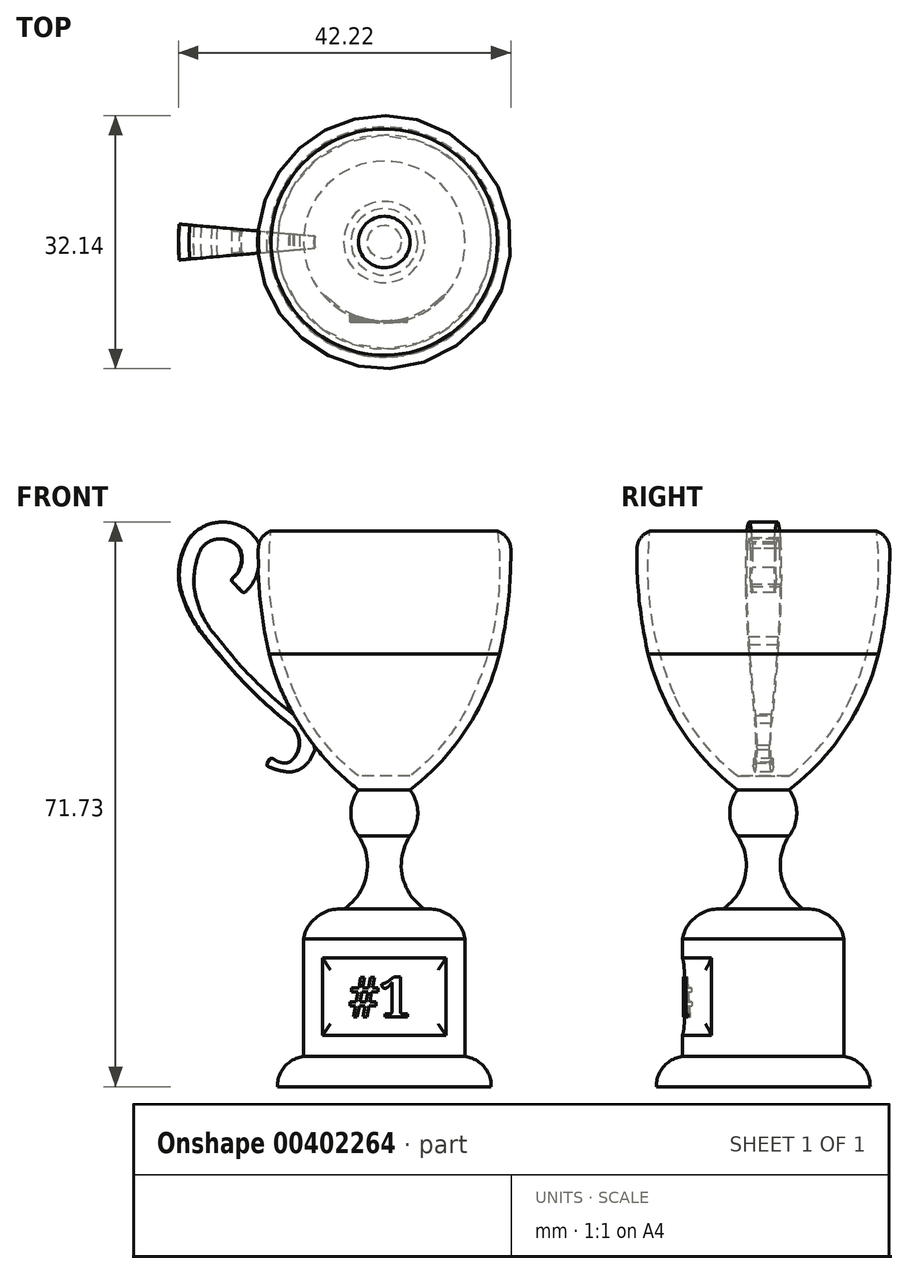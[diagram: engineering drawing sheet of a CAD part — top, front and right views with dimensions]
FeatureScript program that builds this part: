
annotation { "Feature Type Name" : "Feature", "Feature Type Description" : "" }
export const myFeature = defineFeature(function(context is Context, id is Id, definition is map)
    precondition{}
    {
        {
            var Q0;
            Q0=qCreatedBy(makeId("Front.planeOp"),FACE);
            var sketch = newSketch(context, id + "F0", { "sketchPlane" : qUnion([Q0])});
            skArc(sketch, "E0", {"start": v(-16, 36.3) * mm, "mid": v(-15.85, 28.37) * mm, "end": v(-14.63, 20.54) * mm});
            skArc(sketch, "E1", {"start": v(-14.63, 20.54) * mm, "mid": v(-10.4, 10.97) * mm, "end": v(-3.26, 3.3) * mm});
            skArc(sketch, "E2", {"start": v(-3.26, 3.3) * mm, "mid": v(-4.26, 0.37) * mm, "end": v(-3.26, -2.57) * mm});
            skArc(sketch, "E3", {"start": v(-5.16, -11.85) * mm, "mid": v(-2.29, -7.6) * mm, "end": v(-3.26, -2.57) * mm});
            skArc(sketch, "E4", {"start": v(-5.16, -11.85) * mm, "mid": v(-8.46, -12.75) * mm, "end": v(-10.27, -15.64) * mm});
            skLineSegment(sketch, "E5", {"start": v(-10.27, -15.64) * mm, "end": v(-10.27, -30.57) * mm});
            skLineSegment(sketch, "E6", {"start": v(0, -34.4) * mm, "end": v(-13.58, -34.4) * mm});
            skArc(sketch, "E7", {"start": v(-10.27, -30.57) * mm, "mid": v(-12.66, -31.85) * mm, "end": v(-13.58, -34.4) * mm});
            skArc(sketch, "E8", {"start": v(-11.3, 15.41) * mm, "mid": v(-7.94, 9.73) * mm, "end": v(-3.26, 5.06) * mm});
            skArc(sketch, "E9", {"start": v(-14.38, 36.2) * mm, "mid": v(-14.22, 25.6) * mm, "end": v(-11.3, 15.41) * mm});
            skLineSegment(sketch, "E10", {"start": v(-16, 36.3) * mm, "end": v(-14.38, 36.2) * mm});
            skLineSegment(sketch, "E11", {"start": v(-3.26, 5.06) * mm, "end": v(0, 5.06) * mm});
            skLineSegment(sketch, "E12", {"start": v(0, 5.06) * mm, "end": v(0, -34.4) * mm});
            skSolve(sketch);
        }
        {
            var Q0;
            Q0 = qSketchRegion(id + "F0", true);
            var Q1;
            Q1=sQuery(id+"F0.wireOp",EDGE,"E12");
            revolve(context, id + "F1", {"entities" : qUnion([Q0]), "axis" : qUnion([Q1]), "revolveType" : RevolveType.FULL});
        }
        {
            var Q0;
            Q0=qCreatedBy(makeId("Front.planeOp"),FACE);
            var sketch = newSketch(context, id + "F2", { "sketchPlane" : qUnion([Q0])});
            skArc(sketch, "E13", {"start": v(-16.08, 34.82) * mm, "mid": v(-20.32, 37.32) * mm, "end": v(-24.8, 35.27) * mm});
            skArc(sketch, "E14", {"start": v(-24.8, 35.27) * mm, "mid": v(-25.99, 32.28) * mm, "end": v(-26, 29.06) * mm});
            skArc(sketch, "E15", {"start": v(-26, 29.06) * mm, "mid": v(-24.46, 25.14) * mm, "end": v(-22, 21.71) * mm});
            skArc(sketch, "E16", {"start": v(-22, 21.71) * mm, "mid": v(-17.35, 16.43) * mm, "end": v(-12.14, 11.7) * mm});
            skArc(sketch, "E17", {"start": v(-12.14, 6.78) * mm, "mid": v(-10.8, 9.25) * mm, "end": v(-12.14, 11.7) * mm});
            skArc(sketch, "E18", {"start": v(-14.42, 7.47) * mm, "mid": v(-13.37, 6.83) * mm, "end": v(-12.14, 6.78) * mm});
            skLineSegment(sketch, "E19", {"start": v(-14.42, 7.47) * mm, "end": v(-15.02, 6.4) * mm});
            skArc(sketch, "E20", {"start": v(-15.02, 6.4) * mm, "mid": v(-13.59, 5.83) * mm, "end": v(-12.07, 5.57) * mm});
            skArc(sketch, "E21", {"start": v(-12.07, 5.57) * mm, "mid": v(-10.46, 6.12) * mm, "end": v(-9.34, 7.4) * mm});
            skLineSegment(sketch, "E22", {"start": v(-9.34, 7.4) * mm, "end": v(-8.84, 8.4) * mm});
            skLineSegment(sketch, "E23", {"start": v(-8.84, 8.4) * mm, "end": v(-9.04, 9.37) * mm});
            skLineSegment(sketch, "E24", {"start": v(-9.04, 9.37) * mm, "end": v(-11.6, 12.9) * mm});
            skArc(sketch, "E25", {"start": v(-21.31, 22.7) * mm, "mid": v(-16.78, 17.47) * mm, "end": v(-11.6, 12.9) * mm});
            skArc(sketch, "E26", {"start": v(-24.27, 29.36) * mm, "mid": v(-23.34, 25.78) * mm, "end": v(-21.31, 22.7) * mm});
            skArc(sketch, "E27", {"start": v(-23.34, 33.99) * mm, "mid": v(-24.08, 31.73) * mm, "end": v(-24.27, 29.36) * mm});
            skPoint(sketch, "E27.startSnap0", {"position": v(-23.34, 25.78) * mm});
            skArc(sketch, "E28", {"start": v(-18.43, 33.99) * mm, "mid": v(-20.89, 35.2) * mm, "end": v(-23.34, 33.99) * mm});
            skArc(sketch, "E29", {"start": v(-19.57, 29.97) * mm, "mid": v(-18.25, 31.77) * mm, "end": v(-18.43, 33.99) * mm});
            skLineSegment(sketch, "E30", {"start": v(-19.57, 29.97) * mm, "end": v(-17.9, 28.3) * mm});
            skArc(sketch, "E31", {"start": v(-17.9, 28.3) * mm, "mid": v(-16.6, 29.9) * mm, "end": v(-16, 31.86) * mm});
            skArc(sketch, "E32", {"start": v(-16, 31.86) * mm, "mid": v(-15.76, 33.35) * mm, "end": v(-16.08, 34.82) * mm});
            skSolve(sketch);
        }
        {
            var Q0;
            Q0=makeQuery(id+"F2.imprint","IMPRINT",FACE,{"disambiguationData":[TD([[makeQuery(id+"F2.imprint","IMPRINT",EDGE,{"derivedFrom":sQuery(id+"F2.wireOp",EDGE,"E13")}),1.0]])]});
            var Q1;
            Q1=sQuery(id+"F0.wireOp",EDGE,"E12");
            revolve(context, id + "F3", {"operationType" : NewBodyOperationType.ADD, "entities" : qUnion([Q0]), "axis" : qUnion([Q1]), "revolveType" : RevolveType.TWO_DIRECTIONS, "angle" : 5 * degree, "angleBack" : 355 * degree});
        }
        {
            var Q0;
            Q0=makeQuery(id+"F1.opRevolve","SWEPT_EDGE",EDGE,{"disambiguationData":[OSD([sQuery(id+"F0.wireOp",EDGE,"E0"),sQuery(id+"F0.wireOp",EDGE,"E10")])]});
            fillet(context, id + "F4", {"entities" : qUnion([Q0]), "radius" : 2.54 * mm, "tangentPropagation" : true, "allowEdgeOverflow" : false});
        }
        {
            var Q0;
            Q0=makeQuery(id+"F3.opRevolve","SWEPT_EDGE",EDGE,{"disambiguationData":[OSD([sQuery(id+"F2.wireOp",EDGE,"E18"),sQuery(id+"F2.wireOp",EDGE,"E19")])]});
            var Q1;
            Q1=makeQuery(id+"F3.opRevolve","SWEPT_EDGE",EDGE,{"disambiguationData":[OSD([sQuery(id+"F2.wireOp",EDGE,"E19"),sQuery(id+"F2.wireOp",EDGE,"E20")])]});
            var Q2;
            Q2=makeQuery(id+"FtzzwsuBMxib6I8_1.1.F3.opRevolve","SWEPT_EDGE",EDGE,{"disambiguationData":[OSD([sQuery(id+"F2.wireOp",EDGE,"E18"),sQuery(id+"F2.wireOp",EDGE,"E19")])]});
            var Q3;
            Q3=makeQuery(id+"FtzzwsuBMxib6I8_1.1.F3.opRevolve","SWEPT_EDGE",EDGE,{"disambiguationData":[OSD([sQuery(id+"F2.wireOp",EDGE,"E19"),sQuery(id+"F2.wireOp",EDGE,"E20")])]});
            var Q4;
            Q4=makeQuery(id+"FtzzwsuBMxib6I8_1.1.F3.opRevolve","SWEPT_EDGE",EDGE,{"disambiguationData":[OSD([sQuery(id+"F2.wireOp",EDGE,"E29"),sQuery(id+"F2.wireOp",EDGE,"E30")])]});
            var Q5;
            Q5=makeQuery(id+"FtzzwsuBMxib6I8_1.1.F3.opRevolve","SWEPT_EDGE",EDGE,{"disambiguationData":[OSD([sQuery(id+"F2.wireOp",EDGE,"E30"),sQuery(id+"F2.wireOp",EDGE,"E31")])]});
            var Q6;
            Q6=makeQuery(id+"F3.opRevolve","SWEPT_EDGE",EDGE,{"disambiguationData":[OSD([sQuery(id+"F2.wireOp",EDGE,"E30"),sQuery(id+"F2.wireOp",EDGE,"E31")])]});
            var Q7;
            Q7=makeQuery(id+"F3.opRevolve","SWEPT_EDGE",EDGE,{"disambiguationData":[OSD([sQuery(id+"F2.wireOp",EDGE,"E29"),sQuery(id+"F2.wireOp",EDGE,"E30")])]});
            var Q8;
            Q8=makeQuery(id+"F3.opRevolve","CAP_EDGE",EDGE,{"disambiguationData":[OSD([sQuery(id+"F2.wireOp",EDGE,"E30")])],"isStart":false});
            var Q9;
            Q9=makeQuery(id+"F3.opRevolve","CAP_EDGE",EDGE,{"disambiguationData":[OSD([sQuery(id+"F2.wireOp",EDGE,"E30")])],"isStart":true});
            var Q10;
            Q10=makeQuery(id+"F3.opRevolve","CAP_EDGE",EDGE,{"disambiguationData":[OSD([sQuery(id+"F2.wireOp",EDGE,"E19")])],"isStart":false});
            var Q11;
            Q11=makeQuery(id+"F3.opRevolve","CAP_EDGE",EDGE,{"disambiguationData":[OSD([sQuery(id+"F2.wireOp",EDGE,"E19")])],"isStart":true});
            var Q12;
            Q12=makeQuery(id+"FtzzwsuBMxib6I8_1.1.F3.opRevolve","CAP_EDGE",EDGE,{"disambiguationData":[OSD([sQuery(id+"F2.wireOp",EDGE,"E19")])],"isStart":false});
            var Q13;
            Q13=makeQuery(id+"FtzzwsuBMxib6I8_1.1.F3.opRevolve","CAP_EDGE",EDGE,{"disambiguationData":[OSD([sQuery(id+"F2.wireOp",EDGE,"E19")])],"isStart":true});
            var Q14;
            Q14=makeQuery(id+"FtzzwsuBMxib6I8_1.1.F3.opRevolve","CAP_EDGE",EDGE,{"disambiguationData":[OSD([sQuery(id+"F2.wireOp",EDGE,"E30")])],"isStart":false});
            var Q15;
            Q15=makeQuery(id+"FtzzwsuBMxib6I8_1.1.F3.opRevolve","CAP_EDGE",EDGE,{"disambiguationData":[OSD([sQuery(id+"F2.wireOp",EDGE,"E30")])],"isStart":true});
            fillet(context, id + "F5", {"entities" : qUnion([Q0, Q1, Q2, Q3, Q4, Q5, Q6, Q7, Q8, Q9, Q10, Q11, Q12, Q13, Q14, Q15]), "radius" : 0.25 * mm, "tangentPropagation" : true, "allowEdgeOverflow" : false});
        }
        {
            var Q0;
            Q0=qCreatedBy(makeId("Right.planeOp"),FACE);
            var sketch = newSketch(context, id + "F6", { "sketchPlane" : qUnion([Q0])});
            skLineSegment(sketch, "E33.bottom", {"start": v(-10.6, -18.06) * mm, "end": v(-10.04, -18.06) * mm});
            skLineSegment(sketch, "E33.top", {"start": v(-10.6, -27.91) * mm, "end": v(-10.04, -27.91) * mm});
            skLineSegment(sketch, "E33.left", {"start": v(-10.6, -18.06) * mm, "end": v(-10.6, -27.91) * mm});
            skLineSegment(sketch, "E33.right", {"start": v(-10.04, -18.06) * mm, "end": v(-10.04, -27.91) * mm});
            skSolve(sketch);
        }
        {
            var Q0;
            Q0 = qSketchRegion(id + "F6", true);
            var Q1;
            Q1=sQuery(id+"F0.wireOp",EDGE,"E12");
            revolve(context, id + "F7", {"operationType" : NewBodyOperationType.REMOVE, "entities" : qUnion([Q0]), "axis" : qUnion([Q1]), "revolveType" : RevolveType.SYMMETRIC, "oppositeDirection" : true, "angle" : 100 * degree});
        }
        {
            var Q0;
            Q0=makeQuery(id+"F7.boolean.opBoolean","COPY",EDGE,{"derivedFrom":makeQuery(id+"F7.opRevolve","SWEPT_EDGE",EDGE,{"disambiguationData":[OSD([sQuery(id+"F6.wireOp",EDGE,"E33.bottom"),sQuery(id+"F6.wireOp",EDGE,"E33.right")])]})});
            var Q1;
            Q1=makeQuery(id+"F7.boolean.opBoolean","COPY",EDGE,{"derivedFrom":makeQuery(id+"F7.opRevolve","CAP_EDGE",EDGE,{"disambiguationData":[OSD([sQuery(id+"F6.wireOp",EDGE,"E33.right")])],"isStart":true})});
            var Q2;
            Q2=makeQuery(id+"F7.boolean.opBoolean","COPY",EDGE,{"derivedFrom":makeQuery(id+"F7.opRevolve","CAP_EDGE",EDGE,{"disambiguationData":[OSD([sQuery(id+"F6.wireOp",EDGE,"E33.right")])],"isStart":false})});
            var Q3;
            Q3=makeQuery(id+"F7.boolean.opBoolean","COPY",EDGE,{"derivedFrom":makeQuery(id+"F7.opRevolve","SWEPT_EDGE",EDGE,{"disambiguationData":[OSD([sQuery(id+"F6.wireOp",EDGE,"E33.top"),sQuery(id+"F6.wireOp",EDGE,"E33.right")])]})});
            fillet(context, id + "F8", {"entities" : qUnion([Q0, Q1, Q2, Q3]), "radius" : 5.08 * mm, "tangentPropagation" : true, "allowEdgeOverflow" : false});
        }
        {
            var Q0;
            Q0=qCreatedBy(makeId("Front.planeOp"),FACE);
            var sketch = newSketch(context, id + "F9", { "sketchPlane" : qUnion([Q0])});
            skText(sketch, "E34", { "text": "#1", "fontName": "NotoSerif-Bold.ttf"});
            const initialGuessF9  = {"E34": [-0.00457, -0.02554, 1, 0, 0.00508]};
            skSetInitialGuess(sketch, initialGuessF9);
            skSolve(sketch);
        }
        {
            var Q0;
            Q0 = qSketchRegion(id + "F9", true);
            extrude(context, id + "F10", {"entities" : qUnion([Q0]), "operationType" : NewBodyOperationType.ADD, "depth" : 10.16 * mm});
        }
    });
